# Revit family: BV1000
name_source: partatom
category: Plumbing Fixtures
revit_build: Autodesk Revit Structure 2013 (Build: 20120221_2030(x64)
units: mm (PartAtom-declared; Revit-internal decimal feet)

## types (6) — shared parameters
Body Material = Cast iron
Description = Cast iron backwater valve with bronze flapper
Manufacturer = Mifab
Model = BV-1000
URL = www.mifab.com

## per-type parameters (varying)
| type | A | B | Blend for 2 | Blend for B | Blend for Main body 2 | C | C1 | Connection size | HOLE | Hole 1 | Hole 2 | Intake hub | Length of intake | Length of outlet | Mian body 2 | Outlet | Radious | Thickness of upper portion | Upper circle | connection thicknes | main body | uper cover |
| BV1004-4' | 13' - 2 5/16" | 3' - 9" | 3' - 6 19/32" | 3' - 6 19/32" | 5' - 7 1/2" | 3' - 7 1/2" | 3' - 6 17/32" | 2' - 0" | 0' - 2 31/32" | 0' - 10 13/16" | 0' - 9 19/32" | 7' - 5 1/2" | 3' - 9 1/4" | 2' - 7 21/32" | 5' - 9 29/32" | 5' - 8 27/32" | 0' - 9 25/32" | 1' - 7 9/16" | 4' - 1 1/2" | 2' - 2 13/32" | 7' - 7 13/16" | 0' - 7 1/2" |
| BV1002-2' | 10' - 9" | 2' - 9" | 2' - 6 19/32" | 2' - 6 19/32" | 3' - 5 1/4" | 2' - 5 1/4" | 2' - 1 1/2" | 1' - 0" | 0' - 2 3/16" | 0' - 5 13/32" | 0' - 4 13/16" | 6' - 0 29/32" | 3' - 0 27/32" | 2' - 1 13/16" | 3' - 7 21/32" | 4' - 8 3/32" | 0' - 7 3/16" | 1' - 2 11/32" | 3' - 0 5/16" | 1' - 2 13/32" | 5' - 3 5/16" | 0' - 5 1/2" |
| BV1010-10' | 23' - 7 1/2" | 6' - 9" | 6' - 6 19/32" | 6' - 6 19/32" | 12' - 0" | 7' - 0" | 7' - 6" | 5' - 0" | 0' - 5 11/32" | 2' - 3" | 2' - 0" | 13' - 4 1/4" | 6' - 9" | 4' - 8 11/16" | 12' - 2 13/32" | 10' - 3 1/4" | 1' - 5 19/32" | 2' - 11 7/32" | 7' - 5 3/32" | 5' - 2 13/32" | 14' - 4 13/16" | 1' - 1 1/2" |
| BV1003-3' | 11' - 9" | 3' - 4 1/2" | 3' - 2 3/32" | 3' - 2 3/32" | 4' - 10 13/16" | 3' - 4 13/16" | 3' - 1 1/2" | 1' - 6" | 0' - 2 11/16" | 0' - 8 3/32" | 0' - 7 3/16" | 6' - 7 11/16" | 3' - 4 9/32" | 2' - 4 3/16" | 5' - 1 3/16" | 5' - 1 5/16" | 0' - 8 13/16" | 1' - 5 19/32" | 3' - 8 9/16" | 1' - 8 13/32" | 7' - 2 13/32" | 0' - 6 3/4" |
| BV1006-6' | 14' - 9" | 5' - 0" | 4' - 9 19/32" | 4' - 9 19/32" | 8' - 0" | 5' - 0" | 4' - 7 1/2" | 3' - 0" | 0' - 3 31/32" | 1' - 4 3/16" | 1' - 2 13/32" | 8' - 4 1/32" | 4' - 2 9/16" | 2' - 11 13/32" | 8' - 2 13/32" | 6' - 4 31/32" | 1' - 1 1/32" | 2' - 2 3/32" | 5' - 6" | 3' - 2 13/32" | 10' - 4 13/16" | 0' - 10" |
| BV1008-8' | 17' - 0" | 6' - 1 1/2" | 5' - 11 3/32" | 5' - 11 3/32" | 11' - 0" | 7' - 0" | 6' - 6" | 4' - 0" | 0' - 4 27/32" | 1' - 9 19/32" | 1' - 7 3/16" | 9' - 7 5/16" | 4' - 10 9/32" | 3' - 4 13/16" | 11' - 2 13/32" | 7' - 4 11/16" | 1' - 3 31/32" | 2' - 7 31/32" | 6' - 8 27/32" | 4' - 2 13/32" | 14' - 4 13/16" | 1' - 0 1/4" |

## geometry (parser evidence)
native form markers: Blend x3, Sweep x1
no freeform markers — native parametric forms only
